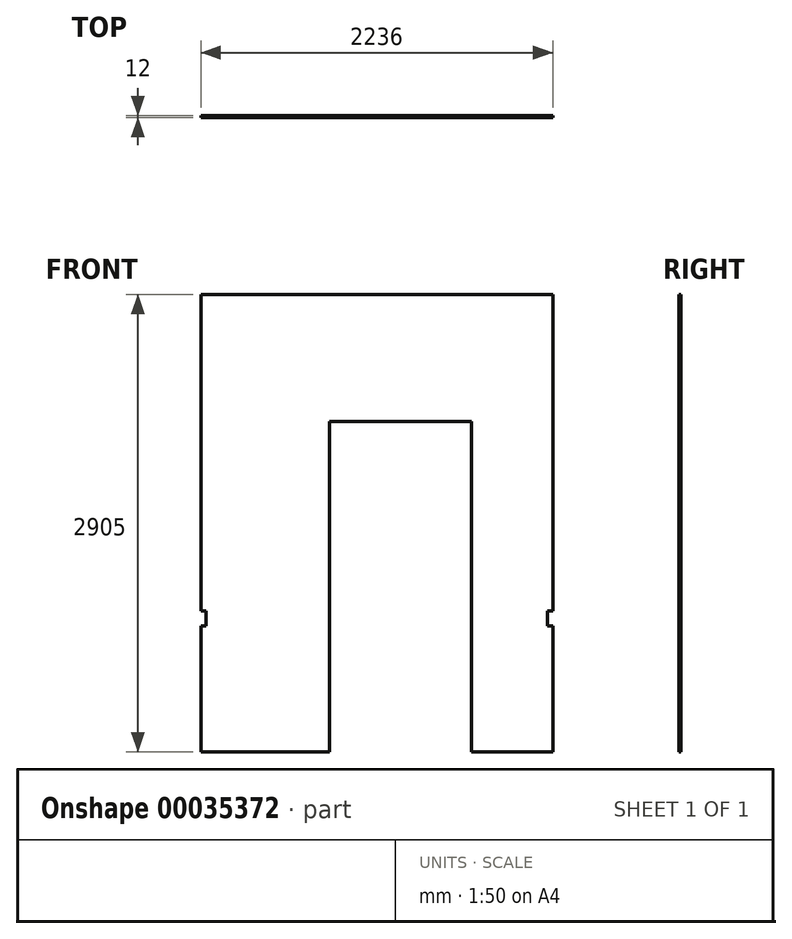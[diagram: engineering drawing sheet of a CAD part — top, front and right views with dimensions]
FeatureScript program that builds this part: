
annotation { "Feature Type Name" : "Feature", "Feature Type Description" : "" }
export const myFeature = defineFeature(function(context is Context, id is Id, definition is map)
    precondition{}
    {
        {
            var Q0;
            Q0=qCreatedBy(makeId("Front.planeOp"),FACE);
            var sketch = newSketch(context, id + "F0", { "sketchPlane" : qUnion([Q0])});
            skLineSegment(sketch, "E0.rect.top", {"start": v(1118, 1452.5) * mm, "end": v(-1118, 1452.5) * mm});
            skLineSegment(sketch, "E0.rect.left", {"start": v(1118, -1452.5) * mm, "end": v(1118, -652.5) * mm});
            skLineSegment(sketch, "E0.rect.right", {"start": v(-1118, -1452.5) * mm, "end": v(-1118, -652.5) * mm});
            skPoint(sketch, "E0.rect.middle", {"position": v(0, 0) * mm});
            skLineSegment(sketch, "E1", {"start": v(-300, -1452.5) * mm, "end": v(-1118, -1452.5) * mm});
            skLineSegment(sketch, "E2", {"start": v(-300, -1452.5) * mm, "end": v(-300, 647.5) * mm});
            skLineSegment(sketch, "E3", {"start": v(-300, 647.5) * mm, "end": v(600, 647.5) * mm});
            skLineSegment(sketch, "E4", {"start": v(600, 647.5) * mm, "end": v(600, -1452.5) * mm});
            skLineSegment(sketch, "E5", {"start": v(600, -1452.5) * mm, "end": v(1118, -1452.5) * mm});
            skLineSegment(sketch, "E6", {"start": v(-1118, -557.5) * mm, "end": v(-1118, 1452.5) * mm});
            skLineSegment(sketch, "E7", {"start": v(1118, -557.5) * mm, "end": v(1118, 1452.5) * mm});
            skLineSegment(sketch, "E8", {"start": v(-1118, -557.5) * mm, "end": v(-1085, -557.5) * mm});
            skLineSegment(sketch, "E9", {"start": v(-1085, -557.5) * mm, "end": v(-1085, -652.5) * mm});
            skLineSegment(sketch, "E10", {"start": v(-1085, -652.5) * mm, "end": v(-1118, -652.5) * mm});
            skLineSegment(sketch, "E11", {"start": v(1118, -557.5) * mm, "end": v(1085, -557.5) * mm});
            skLineSegment(sketch, "E12", {"start": v(1085, -557.5) * mm, "end": v(1085, -652.5) * mm});
            skLineSegment(sketch, "E13", {"start": v(1085, -652.5) * mm, "end": v(1118, -652.5) * mm});
            skSolve(sketch);
        }
        {
            var Q0;
            Q0=makeQuery(id+"F0.imprint","IMPRINT",FACE,{"disambiguationData":[TD([[makeQuery(id+"F0.imprint","IMPRINT",EDGE,{"derivedFrom":sQuery(id+"F0.wireOp",EDGE,"E0.rect.bottom")}),-1.0]])]});
            var Q1;
            Q1=makeQuery(id+"F0.imprint","IMPRINT",FACE,{"disambiguationData":[TD([[makeQuery(id+"F0.imprint","IMPRINT",EDGE,{"derivedFrom":sQuery(id+"F0.wireOp",EDGE,"E0.rect.top")}),1.0]])]});
            extrude(context, id + "F1", {"entities" : qUnion([Q0, Q1]), "depth" : 12 * mm});
        }
    });
